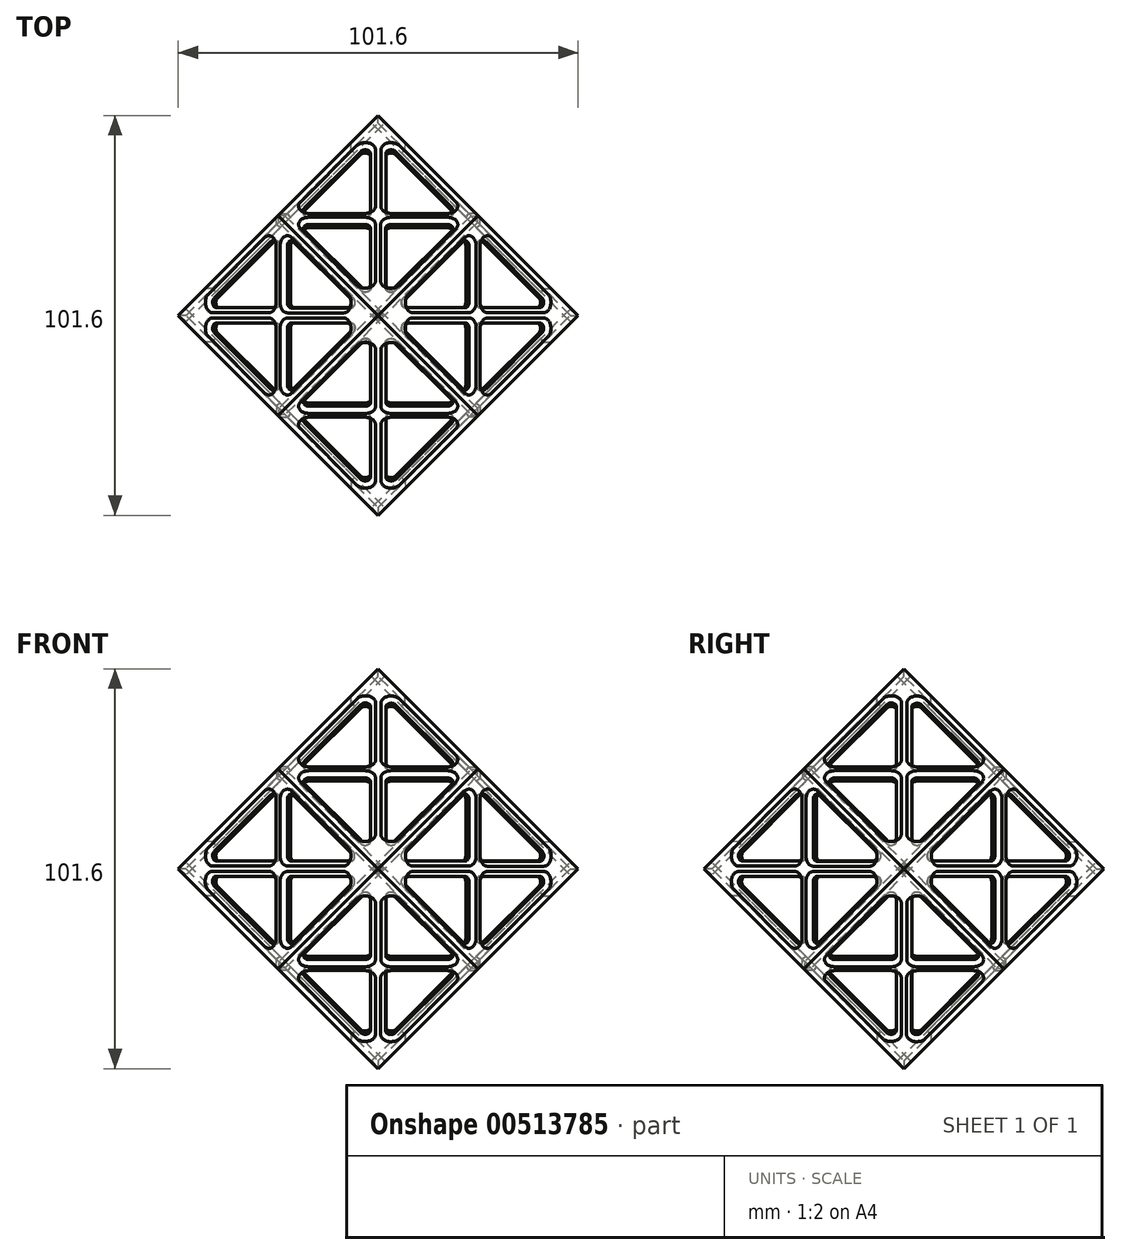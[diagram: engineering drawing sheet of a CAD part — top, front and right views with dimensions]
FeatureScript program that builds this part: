
annotation { "Feature Type Name" : "Feature", "Feature Type Description" : "" }
export const myFeature = defineFeature(function(context is Context, id is Id, definition is map)
    precondition{}
    {
        {
            var Q0;
            Q0=qCreatedBy(makeId("Right.planeOp"),FACE);
            cPlane(context, id + "F0", {"entities" : qUnion([Q0]), "cplaneType" : CPlaneType.OFFSET, "offset" : 25.4 * mm, "width" : 152.4 * mm, "height" : 152.4 * mm});
        }
        {
            var Q0;
            Q0=qCreatedBy(makeId("Right.planeOp"),FACE);
            cPlane(context, id + "F1", {"entities" : qUnion([Q0]), "cplaneType" : CPlaneType.OFFSET, "offset" : 25.4 * mm, "oppositeDirection" : true, "width" : 152.4 * mm, "height" : 152.4 * mm});
        }
        {
            var Q0;
            Q0=qCreatedBy(makeId("Right.planeOp"),FACE);
            var sketch = newSketch(context, id + "F2", { "sketchPlane" : qUnion([Q0])});
            skPoint(sketch, "E0", {"position": v(0, 50.8) * mm});
            skPoint(sketch, "E1", {"position": v(-50.8, 0) * mm});
            skPoint(sketch, "E2", {"position": v(0, -50.8) * mm});
            skPoint(sketch, "E3", {"position": v(50.8, 0) * mm});
            skSolve(sketch);
        }
        {
            var Q0;
            Q0=qCreatedBy(id+"F0.planeOp",FACE);
            var sketch = newSketch(context, id + "F3", { "sketchPlane" : qUnion([Q0])});
            skPoint(sketch, "E4", {"position": v(25.4, 25.4) * mm});
            skPoint(sketch, "E5", {"position": v(25.4, -25.4) * mm});
            skPoint(sketch, "E6", {"position": v(-25.4, -25.4) * mm});
            skPoint(sketch, "E7", {"position": v(-25.4, 25.4) * mm});
            skSolve(sketch);
        }
        {
            var Q0;
            Q0=qCreatedBy(id+"F1.planeOp",FACE);
            var sketch = newSketch(context, id + "F4", { "sketchPlane" : qUnion([Q0])});
            skPoint(sketch, "E8", {"position": v(-25.4, 25.4) * mm});
            skPoint(sketch, "E9", {"position": v(25.4, 25.4) * mm});
            skPoint(sketch, "E10", {"position": v(25.4, -25.4) * mm});
            skPoint(sketch, "E11", {"position": v(-25.4, -25.4) * mm});
            skSolve(sketch);
        }
        {
            var Q0;
            Q0=sQuery(id+"F4.wireOp",VERTEX,"E8");
            var Q1;
            Q1=sQuery(id+"F2.wireOp",VERTEX,"E0");
            var Q2;
            Q2=sQuery(id+"F3.wireOp",VERTEX,"E7");
            cPlane(context, id + "F5", {"entities" : qUnion([Q0, Q1, Q2]), "cplaneType" : CPlaneType.THREE_POINT, "offset" : 25.4 * mm, "width" : 152.4 * mm, "height" : 152.4 * mm});
        }
        {
            var Q0;
            Q0=qCreatedBy(id+"F5.planeOp",FACE);
            var sketch = newSketch(context, id + "F6", { "sketchPlane" : qUnion([Q0])});
            skLineSegment(sketch, "E12", {"start": v(-25.4, 0) * mm, "end": v(0, 35.92) * mm});
            skLineSegment(sketch, "E13", {"start": v(0, 35.92) * mm, "end": v(25.4, 0) * mm});
            skLineSegment(sketch, "E14", {"start": v(25.4, 0) * mm, "end": v(0, -35.92) * mm});
            skLineSegment(sketch, "E15", {"start": v(0, -35.92) * mm, "end": v(-25.4, 0) * mm});
            skLineSegment(sketch, "E16", {"start": v(0, 35.92) * mm, "end": v(0, 0) * mm});
            skLineSegment(sketch, "E17", {"start": v(-25.4, 0) * mm, "end": v(0, 0) * mm});
            skLineSegment(sketch, "E18", {"start": v(0, 0) * mm, "end": v(25.4, 0) * mm});
            skLineSegment(sketch, "E19", {"start": v(0, 0) * mm, "end": v(0, -35.92) * mm});
            skLineSegment(sketch, "E20.0", {"start": v(4.34, 24.29) * mm, "end": v(18.66, 4.04) * mm});
            skLineSegment(sketch, "E21.0", {"start": v(-18.66, 4.04) * mm, "end": v(-4.28, 24.37) * mm});
            skLineSegment(sketch, "E22.1", {"start": v(-4.34, -24.29) * mm, "end": v(-18.66, -4.04) * mm});
            skLineSegment(sketch, "E23.2", {"start": v(18.66, -4.04) * mm, "end": v(4.34, -24.29) * mm});
            skPoint(sketch, "E24.visualSharp", {"position": v(3.17, 25.93) * mm});
            skArc(sketch, "E24.filletArc", {"start": v(4.34, 24.29) * mm, "mid": v(2.92, 24.76) * mm, "end": v(2.03, 23.55) * mm});
            skPoint(sketch, "E25.visualSharp", {"position": v(19.27, 3.18) * mm});
            skArc(sketch, "E25.filletArc", {"start": v(17.62, 2.03) * mm, "mid": v(18.75, 2.72) * mm, "end": v(18.66, 4.04) * mm});
            skPoint(sketch, "E26.visualSharp", {"position": v(19.79, -2.44) * mm});
            skArc(sketch, "E26.filletArc", {"start": v(18.66, -4.04) * mm, "mid": v(18.75, -2.72) * mm, "end": v(17.62, -2.03) * mm});
            skPoint(sketch, "E27.visualSharp", {"position": v(3.7, -25.2) * mm});
            skArc(sketch, "E27.filletArc", {"start": v(2.03, -23.55) * mm, "mid": v(2.92, -24.76) * mm, "end": v(4.34, -24.29) * mm});
            skPoint(sketch, "E28.visualSharp", {"position": v(-2.92, -26.29) * mm});
            skPoint(sketch, "E29.visualSharp", {"position": v(-3.17, -3.18) * mm});
            skPoint(sketch, "E30.visualSharp", {"position": v(-19.01, -3.53) * mm});
            skArc(sketch, "E30.filletArc", {"start": v(-17.62, -2.03) * mm, "mid": v(-18.75, -2.72) * mm, "end": v(-18.66, -4.04) * mm});
            skPoint(sketch, "E31.visualSharp", {"position": v(-19.27, 3.17) * mm});
            skArc(sketch, "E31.filletArc", {"start": v(-18.66, 4.04) * mm, "mid": v(-18.75, 2.72) * mm, "end": v(-17.62, 2.03) * mm});
            skPoint(sketch, "E32.visualSharp", {"position": v(-3.17, 3.17) * mm});
            skPoint(sketch, "E33.visualSharp", {"position": v(-3.17, 25.93) * mm});
            skArc(sketch, "E33.filletArc", {"start": v(-1.97, 23.63) * mm, "mid": v(-2.86, 24.84) * mm, "end": v(-4.28, 24.37) * mm});
            skLineSegment(sketch, "E34", {"start": v(17.62, 2.03) * mm, "end": v(3.3, 2.03) * mm});
            skLineSegment(sketch, "E35", {"start": v(2.03, 3.3) * mm, "end": v(2.03, 23.55) * mm});
            skPoint(sketch, "E36.visualSharp", {"position": v(2.03, 2.03) * mm});
            skArc(sketch, "E36.filletArc", {"start": v(2.03, 3.3) * mm, "mid": v(2.4, 2.4) * mm, "end": v(3.3, 2.03) * mm});
            skLineSegment(sketch, "E37", {"start": v(17.62, -2.03) * mm, "end": v(3.3, -2.03) * mm});
            skLineSegment(sketch, "E38", {"start": v(2.03, -3.3) * mm, "end": v(2.03, -23.55) * mm});
            skLineSegment(sketch, "E39", {"start": v(-2.03, -23.55) * mm, "end": v(-2.03, -3.3) * mm});
            skLineSegment(sketch, "E40", {"start": v(-3.3, -2.03) * mm, "end": v(-17.62, -2.03) * mm});
            skLineSegment(sketch, "E41", {"start": v(-17.62, 2.03) * mm, "end": v(-3.24, 2.03) * mm});
            skLineSegment(sketch, "E42", {"start": v(-1.97, 3.3) * mm, "end": v(-1.97, 23.63) * mm});
            skPoint(sketch, "E43.visualSharp", {"position": v(2.03, -2.03) * mm});
            skArc(sketch, "E43.filletArc", {"start": v(3.3, -2.03) * mm, "mid": v(2.4, -2.4) * mm, "end": v(2.03, -3.3) * mm});
            skPoint(sketch, "E44.visualSharp", {"position": v(-2.03, -2.03) * mm});
            skArc(sketch, "E44.filletArc", {"start": v(-2.03, -3.3) * mm, "mid": v(-2.4, -2.4) * mm, "end": v(-3.3, -2.03) * mm});
            skPoint(sketch, "E45.visualSharp", {"position": v(-1.97, 2.03) * mm});
            skArc(sketch, "E45.filletArc", {"start": v(-3.24, 2.03) * mm, "mid": v(-2.35, 2.4) * mm, "end": v(-1.97, 3.3) * mm});
            skArc(sketch, "E46.filletArc", {"start": v(-4.34, -24.29) * mm, "mid": v(-2.92, -24.76) * mm, "end": v(-2.03, -23.55) * mm});
            skSolve(sketch);
        }
        {
            var Q0;
            Q0=makeQuery(id+"F6.imprint","IMPRINT",FACE,{"disambiguationData":[TD([[makeQuery(id+"F6.imprint","IMPRINT",EDGE,{"derivedFrom":sQuery(id+"F6.wireOp",EDGE,"E12")}),-1.0]])]});
            var Q1;
            Q1=makeQuery(id+"F6.imprint","IMPRINT",FACE,{"disambiguationData":[TD([[makeQuery(id+"F6.imprint","IMPRINT",EDGE,{"derivedFrom":sQuery(id+"F6.wireOp",EDGE,"E13")}),-1.0]])]});
            var Q2;
            Q2=makeQuery(id+"F6.imprint","IMPRINT",FACE,{"disambiguationData":[TD([[makeQuery(id+"F6.imprint","IMPRINT",EDGE,{"derivedFrom":sQuery(id+"F6.wireOp",EDGE,"E14")}),-1.0]])]});
            var Q3;
            Q3=makeQuery(id+"F6.imprint","IMPRINT",FACE,{"disambiguationData":[TD([[makeQuery(id+"F6.imprint","IMPRINT",EDGE,{"derivedFrom":sQuery(id+"F6.wireOp",EDGE,"E15")}),-1.0]])]});
            extrude(context, id + "F7", {"entities" : qUnion([Q0, Q1, Q2, Q3]), "oppositeDirection" : true, "depth" : 2.54 * mm, "hasDraft" : true, "draftAngle" : 3 * degree, "draftPullDirection" : true});
        }
        {
            var Q0;
            Q0=makeQuery(id+"F7.opExtrude","CAP_EDGE",EDGE,{"disambiguationData":[OSD([sQuery(id+"F6.wireOp",EDGE,"E21.0")])],"isStart":true});
            var Q1;
            Q1=makeQuery(id+"F7.opExtrude","CAP_EDGE",EDGE,{"disambiguationData":[OSD([sQuery(id+"F6.wireOp",EDGE,"E20.1")])],"isStart":true});
            var Q2;
            Q2=makeQuery(id+"F7.opExtrude","CAP_EDGE",EDGE,{"disambiguationData":[OSD([sQuery(id+"F6.wireOp",EDGE,"E23.1")])],"isStart":true});
            var Q3;
            Q3=makeQuery(id+"F7.opExtrude","CAP_EDGE",EDGE,{"disambiguationData":[OSD([sQuery(id+"F6.wireOp",EDGE,"E22.0")])],"isStart":true});
            var Q4;
            Q4=makeQuery(id+"F7.opExtrude","CAP_EDGE",EDGE,{"disambiguationData":[OSD([sQuery(id+"F6.wireOp",EDGE,"E43.filletArc")])],"isStart":true});
            var Q5;
            Q5=makeQuery(id+"F7.opExtrude","CAP_EDGE",EDGE,{"disambiguationData":[OSD([sQuery(id+"F6.wireOp",EDGE,"E35")])],"isStart":true});
            var Q6;
            Q6=makeQuery(id+"F7.opExtrude","CAP_EDGE",EDGE,{"disambiguationData":[OSD([sQuery(id+"F6.wireOp",EDGE,"E40")])],"isStart":true});
            chamfer(context, id + "F8", {"entities" : qUnion([Q0, Q1, Q2, Q3, Q4, Q5, Q6]), "width" : 1.27 * mm, "tangentPropagation" : true});
        }
        {
            var Q0;
            Q0=qCreatedBy(makeId("Front.planeOp"),FACE);
            var sketch = newSketch(context, id + "F9", { "sketchPlane" : qUnion([Q0])});
            skLineSegment(sketch, "E47", {"start": v(0, 50.8) * mm, "end": v(0, -50.8) * mm, "construction": true});
            skSolve(sketch);
        }
        {
            var Q0;
            Q0=makeQuery(id+"F7.opExtrude","SWEPT_BODY",BODY,{"disambiguationData":[OSD([sQuery(id+"F6.wireOp",EDGE,"E12"),sQuery(id+"F6.wireOp",EDGE,"E13"),sQuery(id+"F6.wireOp",EDGE,"E14"),sQuery(id+"F6.wireOp",EDGE,"E15")])]});
            var Q1;
            Q1=sQuery(id+"F9.wireOp",EDGE,"E47");
            circularPattern(context, id + "F10", {"entities" : qUnion([Q0]), "axis" : qUnion([Q1]), "angle" : 360 * degree, "instanceCount" : 4, "equalSpace" : true});
        }
        {
            var Q0;
            Q0=qCreatedBy(makeId("Right.planeOp"),FACE);
            var sketch = newSketch(context, id + "F11", { "sketchPlane" : qUnion([Q0])});
            skLineSegment(sketch, "E48", {"start": v(50.8, 0) * mm, "end": v(-50.8, 0) * mm, "construction": true});
            skSolve(sketch);
        }
        {
            var Q0;
            Q0=makeQuery(id+"F10.opPattern","COPY",BODY,{"derivedFrom":makeQuery(id+"F7.opExtrude","SWEPT_BODY",BODY,{"disambiguationData":[OSD([sQuery(id+"F6.wireOp",EDGE,"E12"),sQuery(id+"F6.wireOp",EDGE,"E13"),sQuery(id+"F6.wireOp",EDGE,"E14"),sQuery(id+"F6.wireOp",EDGE,"E15")])]}),"instanceName":"2"});
            var Q1;
            Q1=sQuery(id+"F11.wireOp",EDGE,"E48");
            circularPattern(context, id + "F12", {"entities" : qUnion([Q0]), "axis" : qUnion([Q1]), "angle" : 360 * degree, "instanceCount" : 4, "equalSpace" : true});
        }
        {
            var Q0;
            Q0=makeQuery(id+"F7.opExtrude","SWEPT_BODY",BODY,{"disambiguationData":[OSD([sQuery(id+"F6.wireOp",EDGE,"E12"),sQuery(id+"F6.wireOp",EDGE,"E13"),sQuery(id+"F6.wireOp",EDGE,"E14"),sQuery(id+"F6.wireOp",EDGE,"E15")])]});
            var Q1;
            Q1=sQuery(id+"F11.wireOp",EDGE,"E48");
            circularPattern(context, id + "F13", {"entities" : qUnion([Q0]), "axis" : qUnion([Q1]), "angle" : 360 * degree, "instanceCount" : 4, "equalSpace" : true});
        }
        {
            var Q0;
            Q0=qCreatedBy(makeId("Front.planeOp"),FACE);
            var sketch = newSketch(context, id + "F14", { "sketchPlane" : qUnion([Q0])});
            skLineSegment(sketch, "E49", {"start": v(0, 50.8) * mm, "end": v(0, -50.8) * mm, "construction": true});
            skSolve(sketch);
        }
        {
            var Q0;
            Q0=makeQuery(id+"F12.opPattern","COPY",BODY,{"derivedFrom":makeQuery(id+"F10.opPattern","COPY",BODY,{"derivedFrom":makeQuery(id+"F7.opExtrude","SWEPT_BODY",BODY,{"disambiguationData":[OSD([sQuery(id+"F6.wireOp",EDGE,"E12"),sQuery(id+"F6.wireOp",EDGE,"E13"),sQuery(id+"F6.wireOp",EDGE,"E14"),sQuery(id+"F6.wireOp",EDGE,"E15")])]}),"instanceName":"2"}),"instanceName":"2"});
            var Q1;
            Q1=sQuery(id+"F14.wireOp",EDGE,"E49");
            circularPattern(context, id + "F15", {"entities" : qUnion([Q0]), "axis" : qUnion([Q1]), "angle" : 90 * degree, "instanceCount" : 2, "equalSpace" : true});
        }
        {
            var Q0;
            Q0=makeQuery(id+"F12.opPattern","COPY",BODY,{"derivedFrom":makeQuery(id+"F10.opPattern","COPY",BODY,{"derivedFrom":makeQuery(id+"F7.opExtrude","SWEPT_BODY",BODY,{"disambiguationData":[OSD([sQuery(id+"F6.wireOp",EDGE,"E12"),sQuery(id+"F6.wireOp",EDGE,"E13"),sQuery(id+"F6.wireOp",EDGE,"E14"),sQuery(id+"F6.wireOp",EDGE,"E15")])]}),"instanceName":"2"}),"instanceName":"2"});
            var Q1;
            Q1=sQuery(id+"F14.wireOp",EDGE,"E49");
            circularPattern(context, id + "F16", {"entities" : qUnion([Q0]), "axis" : qUnion([Q1]), "angle" : 90 * degree, "instanceCount" : 2, "oppositeDirection" : true, "equalSpace" : true});
        }
    });
